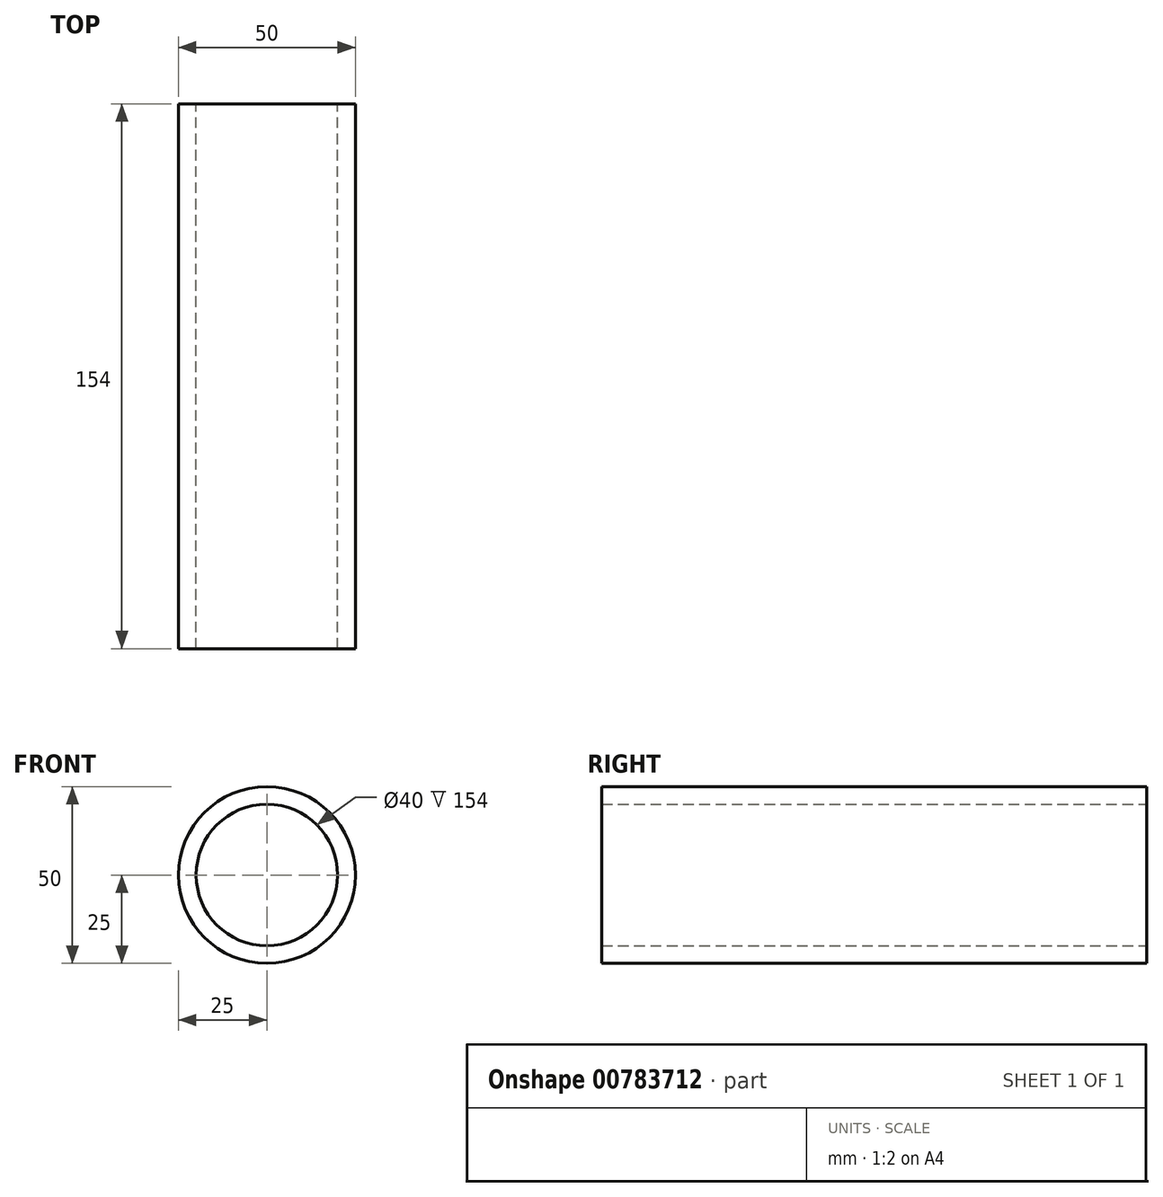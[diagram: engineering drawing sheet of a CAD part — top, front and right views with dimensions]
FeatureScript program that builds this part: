
annotation { "Feature Type Name" : "Feature", "Feature Type Description" : "" }
export const myFeature = defineFeature(function(context is Context, id is Id, definition is map)
    precondition{}
    {
        {
            var Q0;
            Q0=qCreatedBy(makeId("Front.planeOp"),FACE);
            var sketch = newSketch(context, id + "F0", { "sketchPlane" : qUnion([Q0])});
            skCircle(sketch, "E0", {"center": v(0, 0) * mm, "radius": 25 * mm});
            skCircle(sketch, "E1", {"center": v(0, 0) * mm, "radius": 20 * mm});
            skSolve(sketch);
        }
        {
            var Q0;
            Q0=makeQuery(id+"F0.imprint","IMPRINT",FACE,{"disambiguationData":[TD([[makeQuery(id+"F0.imprint","IMPRINT",EDGE,{"derivedFrom":sQuery(id+"F0.wireOp",EDGE,"E0")}),1.0]])]});
            extrude(context, id + "F1", {"entities" : qUnion([Q0]), "depth" : 154 * mm, "offsetDistance" : 25 * mm});
        }
    });
